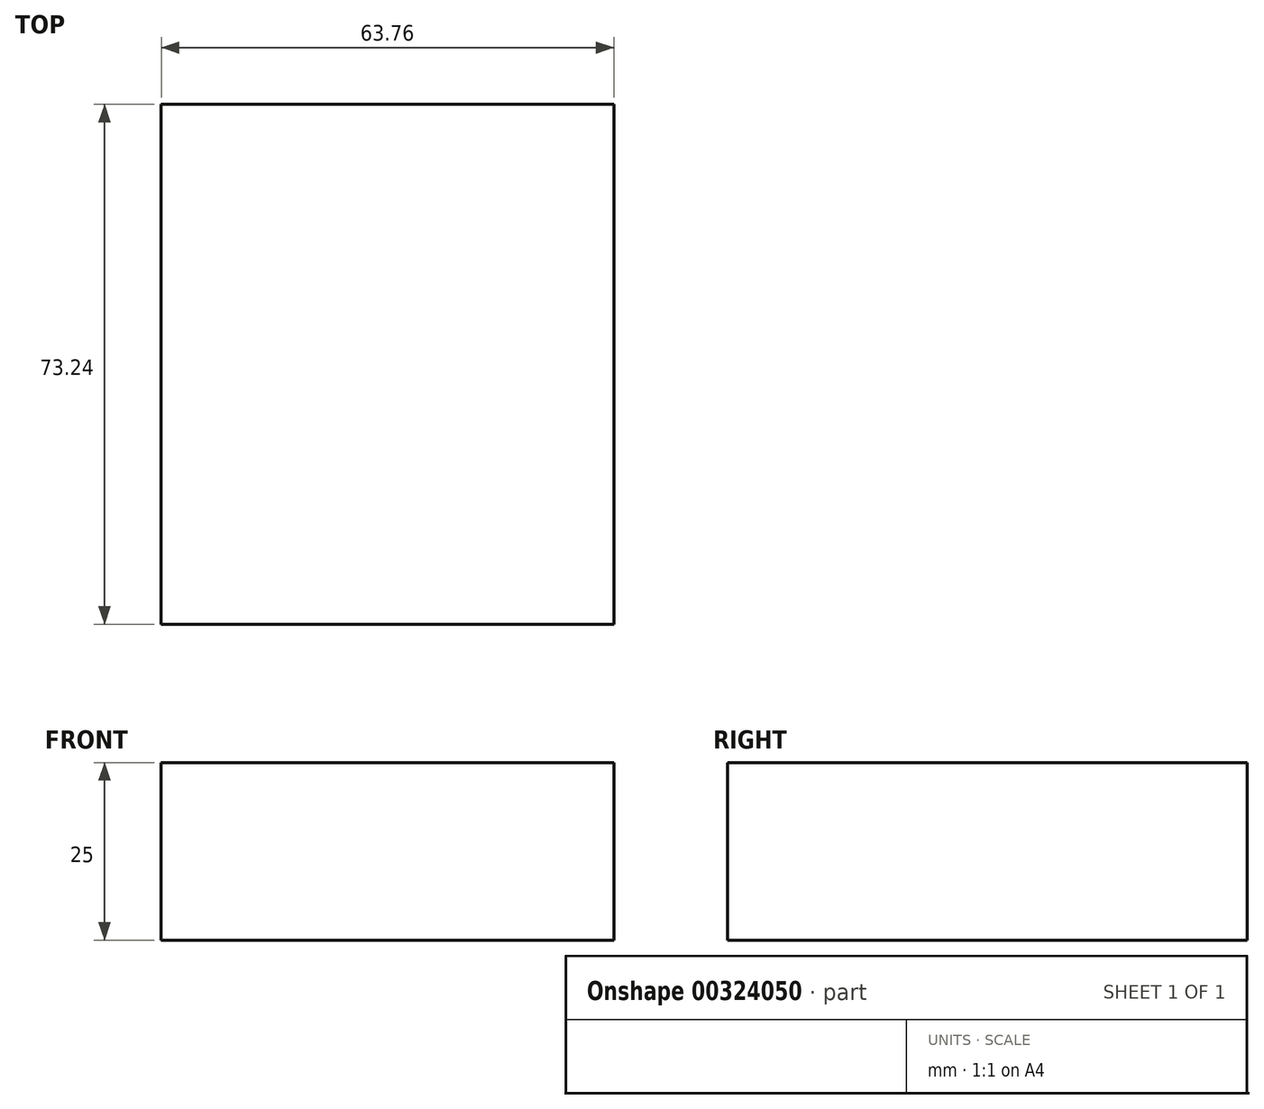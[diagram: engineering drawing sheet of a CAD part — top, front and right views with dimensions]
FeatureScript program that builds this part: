
annotation { "Feature Type Name" : "Feature", "Feature Type Description" : "" }
export const myFeature = defineFeature(function(context is Context, id is Id, definition is map)
    precondition{}
    {
        {
            var Q0;
            Q0=qCreatedBy(makeId("Top.planeOp"),FACE);
            var sketch = newSketch(context, id + "F0", { "sketchPlane" : qUnion([Q0])});
            skLineSegment(sketch, "E0.bottom", {"start": v(-105.84, -69.04) * mm, "end": v(-42.08, -69.04) * mm});
            skLineSegment(sketch, "E0.top", {"start": v(-105.84, 4.2) * mm, "end": v(-42.08, 4.2) * mm});
            skLineSegment(sketch, "E0.left", {"start": v(-105.84, -69.04) * mm, "end": v(-105.84, 4.2) * mm});
            skLineSegment(sketch, "E0.right", {"start": v(-42.08, -69.04) * mm, "end": v(-42.08, 4.2) * mm});
            skSolve(sketch);
        }
        {
            var Q0;
            Q0 = qSketchRegion(id + "F0", true);
            extrude(context, id + "F1", {"entities" : qUnion([Q0]), "depth" : 25 * mm});
        }
    });
